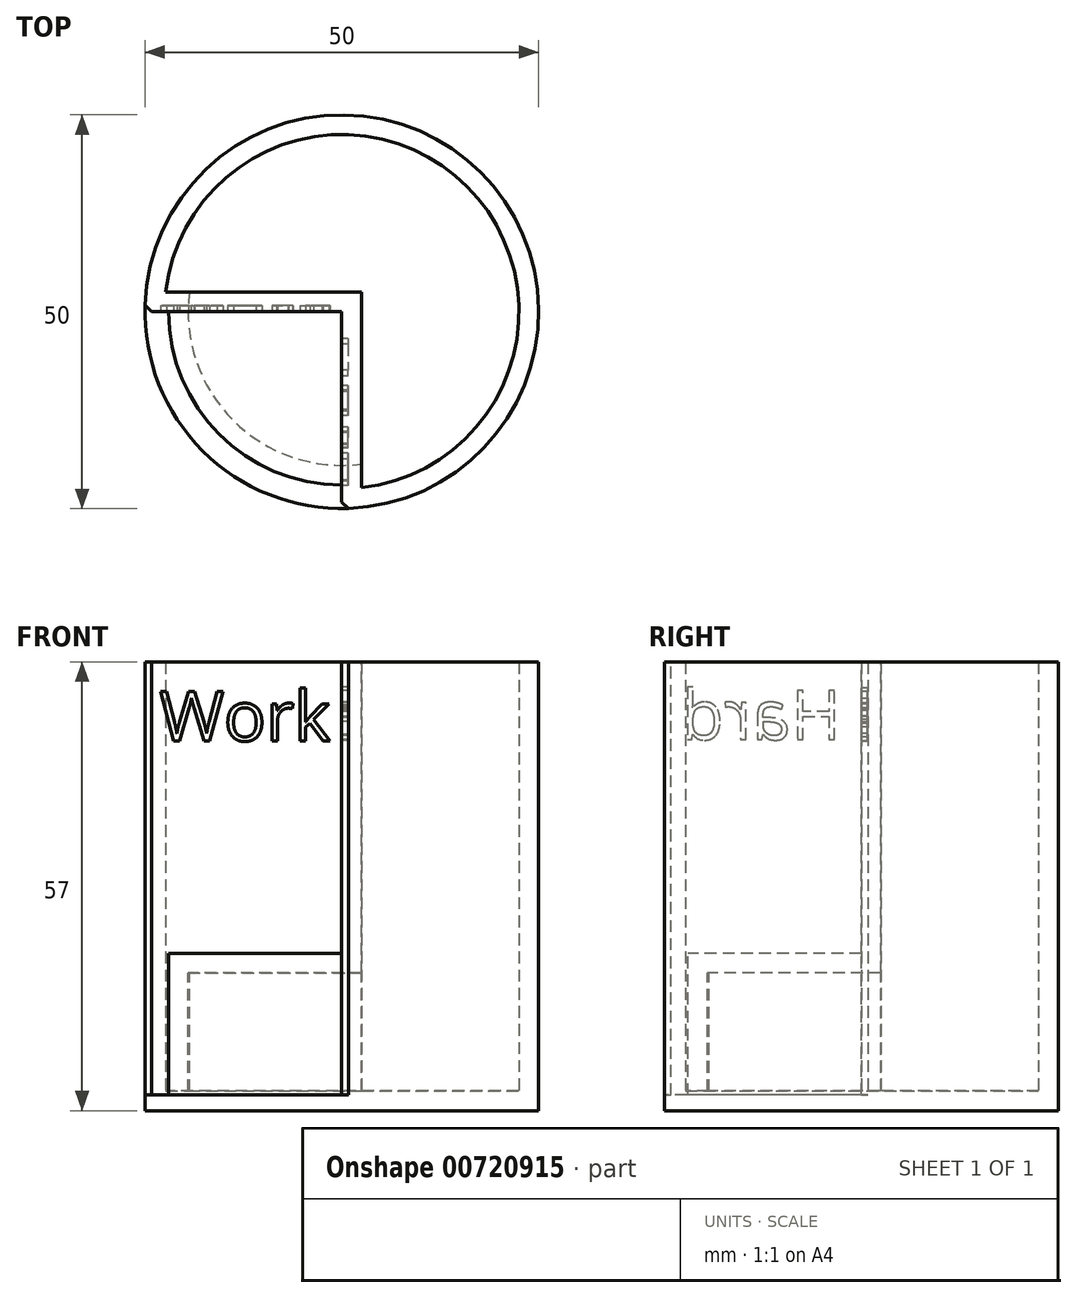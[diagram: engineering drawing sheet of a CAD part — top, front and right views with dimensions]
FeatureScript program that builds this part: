
annotation { "Feature Type Name" : "Feature", "Feature Type Description" : "" }
export const myFeature = defineFeature(function(context is Context, id is Id, definition is map)
    precondition{}
    {
        {
            var Q0;
            Q0=qCreatedBy(makeId("Top.planeOp"),FACE);
            var sketch = newSketch(context, id + "F0", { "sketchPlane" : qUnion([Q0])});
            skCircle(sketch, "E0", {"center": v(0, 0) * mm, "radius": 25 * mm});
            skSolve(sketch);
        }
        {
            var Q0;
            Q0=makeQuery(id+"F0.imprint","IMPRINT",FACE,{"disambiguationData":[TD([[makeQuery(id+"F0.imprint","IMPRINT",EDGE,{"derivedFrom":sQuery(id+"F0.wireOp",EDGE,"E0")}),1.0]])]});
            extrude(context, id + "F1", {"entities" : qUnion([Q0]), "depth" : 50 * mm, "offsetDistance" : 25 * mm});
        }
        {
            var Q0;
            Q0=makeQuery(id+"F1.opExtrude","CAP_FACE",FACE,{"disambiguationData":[OSD([sQuery(id+"F0.wireOp",EDGE,"E0")])],"isStart":false});
            var sketch = newSketch(context, id + "F2", { "sketchPlane" : qUnion([Q0])});
            skLineSegment(sketch, "E1.bottom", {"start": v(0, 0) * mm, "end": v(-35.4, 0) * mm});
            skLineSegment(sketch, "E1.top", {"start": v(0, -37.42) * mm, "end": v(-35.4, -37.42) * mm});
            skLineSegment(sketch, "E1.left", {"start": v(0, 0) * mm, "end": v(0, -37.42) * mm});
            skLineSegment(sketch, "E1.right", {"start": v(-35.4, 0) * mm, "end": v(-35.4, -37.42) * mm});
            skSolve(sketch);
        }
        {
            var Q0;
            {var subQ0=sQuery(id+"F2.wireOp",EDGE,"E1.left");var subQ1=sQuery(id+"F2.wireOp",EDGE,"E1.bottom");var subQ2=makeQuery(id+"F2.imprint","INTERSECT",VERTEX,{"derivedFrom":[subQ1,subQ0]});Q0=makeQuery(id+"F2.imprint","IMPRINT",FACE,{"disambiguationData":[TD([[makeQuery(id+"F2.imprint","IMPRINT",EDGE,{"disambiguationData":[TD([[subQ2,-1.0]])],"derivedFrom":subQ1}),1.0]])]});}
            extrude(context, id + "F3", {"entities" : qUnion([Q0]), "operationType" : NewBodyOperationType.REMOVE, "oppositeDirection" : true, "depth" : 30 * mm, "offsetDistance" : 25 * mm});
        }
        {
            var Q0;
            Q0=makeQuery(id+"F3.boolean.opBoolean","COPY",FACE,{"derivedFrom":makeQuery(id+"F3.opExtrude","CAP_FACE",FACE,{"disambiguationData":[OSD([sQuery(id+"F0.wireOp",EDGE,"E0"),sQuery(id+"F2.wireOp",EDGE,"E1.bottom"),sQuery(id+"F2.wireOp",EDGE,"E1.left")])],"isStart":false})});
            var sketch = newSketch(context, id + "F4", { "sketchPlane" : qUnion([Q0])});
            skArc(sketch, "E2", {"start": v(0, -22.02) * mm, "mid": v(-15.57, -15.57) * mm, "end": v(-22.02, 0) * mm});
            skSolve(sketch);
        }
        {
            var Q0;
            {var subQ0=sQuery(id+"F4.wireOp",EDGE,"E2");Q0=makeQuery(id+"F4.imprint","IMPRINT",FACE,{"disambiguationData":[TD([[makeQuery(id+"F4.imprint","IMPRINT",EDGE,{"derivedFrom":subQ0}),-1.0]])]});}
            var Q1;
            Q1=makeQuery(id+"F1.opExtrude","CAP_FACE",FACE,{"disambiguationData":[OSD([sQuery(id+"F0.wireOp",EDGE,"E0")])],"isStart":false});
            extrude(context, id + "F5", {"entities" : qUnion([Q0, Q1]), "operationType" : NewBodyOperationType.REMOVE, "oppositeDirection" : true, "depth" : 18 * mm, "offsetDistance" : 25 * mm});
        }
        {
            var Q0;
            Q0=makeQuery(id+"F5.boolean.opBoolean","COPY",FACE,{"derivedFrom":makeQuery(id+"F5.opExtrude","CAP_FACE",FACE,{"disambiguationData":[OSD([sQuery(id+"F0.wireOp",EDGE,"E0")])],"isStart":false})});
            shell(context, id + "F6", {"entities" : qUnion([Q0]), "thickness" : 2.5 * mm});
        }
        {
            var Q0;
            Q0=makeQuery(id+"F5.boolean.opBoolean","COPY",FACE,{"derivedFrom":makeQuery(id+"F5.opExtrude","CAP_FACE",FACE,{"disambiguationData":[OSD([sQuery(id+"F0.wireOp",EDGE,"E0")])],"isStart":false})});
            extrude(context, id + "F7", {"entities" : qUnion([Q0]), "operationType" : NewBodyOperationType.ADD, "depth" : 25 * mm, "offsetDistance" : 25 * mm});
        }
        {
            var Q0;
            Q0=makeQuery(id+"F3.boolean.opBoolean","COPY",EDGE,{"derivedFrom":makeQuery(id+"F3.opExtrude","CAP_EDGE",EDGE,{"disambiguationData":[OSD([sQuery(id+"F0.wireOp",EDGE,"E0")])],"isStart":false})});
            var Q1;
            Q1=makeQuery(id+"F5.boolean.opBoolean","COPY",EDGE,{"derivedFrom":makeQuery(id+"F5.opExtrude","CAP_EDGE",EDGE,{"disambiguationData":[OSD([sQuery(id+"F4.wireOp",EDGE,"E2")])],"isStart":true})});
            var Q2;
            {var subQ0=sQuery(id+"F2.wireOp",EDGE,"E1.left");var subQ1=sQuery(id+"F0.wireOp",EDGE,"E0");Q2=makeQuery(id+"F7.boolean.opBoolean","MERGE",EDGE,{"derivedFrom":[makeQuery(id+"F3.boolean.opBoolean","COPY",EDGE,{"derivedFrom":makeQuery(id+"F3.opExtrude","SWEPT_EDGE",EDGE,{"disambiguationData":[OSD([subQ1,subQ0])]})}),makeQuery(id+"F7.opExtrude","SWEPT_EDGE",EDGE,{"disambiguationData":[OSD([subQ1,subQ0]),TDD([makeQuery(id+"F5.boolean.opBoolean","COPY",VERTEX,{"derivedFrom":makeQuery(id+"F5.opExtrude","CAP_VERTEX",VERTEX,{"disambiguationData":[OSD([subQ1,subQ0])],"isStart":false})})])]})]});}
            var Q3;
            {var subQ0=sQuery(id+"F2.wireOp",EDGE,"E1.bottom");var subQ1=sQuery(id+"F0.wireOp",EDGE,"E0");Q3=makeQuery(id+"F7.boolean.opBoolean","MERGE",EDGE,{"derivedFrom":[makeQuery(id+"F3.boolean.opBoolean","COPY",EDGE,{"derivedFrom":makeQuery(id+"F3.opExtrude","SWEPT_EDGE",EDGE,{"disambiguationData":[OSD([subQ1,subQ0])]})}),makeQuery(id+"F7.opExtrude","SWEPT_EDGE",EDGE,{"disambiguationData":[OSD([subQ1,subQ0]),TDD([makeQuery(id+"F5.boolean.opBoolean","COPY",VERTEX,{"derivedFrom":makeQuery(id+"F5.opExtrude","CAP_VERTEX",VERTEX,{"disambiguationData":[OSD([subQ1,subQ0])],"isStart":false})})])]})]});}
            var Q4;
            {var subQ0=sQuery(id+"F2.wireOp",EDGE,"E1.bottom");Q4=makeQuery(id+"F7.opExtrude","CAP_EDGE",EDGE,{"disambiguationData":[OSD([subQ0]),TDD([makeQuery(id+"F5.boolean.opBoolean","COPY",EDGE,{"derivedFrom":makeQuery(id+"F5.opExtrude","CAP_EDGE",EDGE,{"disambiguationData":[OSD([subQ0]),TDD([makeQuery(id+"F3.boolean.opBoolean","COPY",EDGE,{"derivedFrom":makeQuery(id+"F3.opExtrude","CAP_EDGE",EDGE,{"disambiguationData":[OSD([subQ0])],"isStart":true})})])],"isStart":false})})])],"isStart":false});}
            var Q5;
            {var subQ0=sQuery(id+"F2.wireOp",EDGE,"E1.left");Q5=makeQuery(id+"F7.opExtrude","CAP_EDGE",EDGE,{"disambiguationData":[OSD([subQ0]),TDD([makeQuery(id+"F5.boolean.opBoolean","COPY",EDGE,{"derivedFrom":makeQuery(id+"F5.opExtrude","CAP_EDGE",EDGE,{"disambiguationData":[OSD([subQ0]),TDD([makeQuery(id+"F3.boolean.opBoolean","COPY",EDGE,{"derivedFrom":makeQuery(id+"F3.opExtrude","CAP_EDGE",EDGE,{"disambiguationData":[OSD([subQ0])],"isStart":true})})])],"isStart":false})})])],"isStart":false});}
            var Q6;
            {var subQ0=sQuery(id+"F2.wireOp",EDGE,"E1.left");Q6=makeQuery(id+"F7.opExtrude","CAP_EDGE",EDGE,{"disambiguationData":[OSD([subQ0]),TDD([makeQuery(id+"F6.opShell","OFFSET_EDGE",EDGE,{"disambiguationData":[OSD([subQ0])]})])],"isStart":false});}
            var Q7;
            {var subQ0=sQuery(id+"F0.wireOp",EDGE,"E0");Q7=makeQuery(id+"F7.opExtrude","CAP_EDGE",EDGE,{"disambiguationData":[OSD([subQ0]),TDD([makeQuery(id+"F6.opShell","OFFSET_EDGE",EDGE,{"disambiguationData":[OSD([subQ0]),TDD([makeQuery(id+"F5.boolean.opBoolean","COPY",EDGE,{"derivedFrom":makeQuery(id+"F5.opExtrude","CAP_EDGE",EDGE,{"disambiguationData":[OSD([subQ0])],"isStart":false})})])]})])],"isStart":false});}
            var Q8;
            {var subQ0=sQuery(id+"F0.wireOp",EDGE,"E0");Q8=makeQuery(id+"F7.opExtrude","CAP_EDGE",EDGE,{"disambiguationData":[OSD([subQ0]),TDD([makeQuery(id+"F5.boolean.opBoolean","COPY",EDGE,{"derivedFrom":makeQuery(id+"F5.opExtrude","CAP_EDGE",EDGE,{"disambiguationData":[OSD([subQ0])],"isStart":false})})])],"isStart":false});}
            var Q9;
            {var subQ0=sQuery(id+"F2.wireOp",EDGE,"E1.bottom");Q9=makeQuery(id+"F7.opExtrude","CAP_EDGE",EDGE,{"disambiguationData":[OSD([subQ0]),TDD([makeQuery(id+"F6.opShell","OFFSET_EDGE",EDGE,{"disambiguationData":[OSD([subQ0])]})])],"isStart":false});}
            chamfer(context, id + "F8", {"entities" : qUnion([Q0, Q1, Q2, Q3, Q4, Q5, Q6, Q7, Q8, Q9]), "width" : 0.8 * mm, "tangentPropagation" : true});
        }
        {
            var Q0;
            {var subQ0=sQuery(id+"F2.wireOp",EDGE,"E1.left");var subQ1=makeQuery(id+"F3.boolean.opBoolean","COPY",EDGE,{"derivedFrom":makeQuery(id+"F3.opExtrude","CAP_EDGE",EDGE,{"disambiguationData":[OSD([subQ0])],"isStart":false})});Q0=makeQuery(id+"F7.boolean.opBoolean","MERGE",FACE,{"derivedFrom":[makeQuery(id+"F5.boolean.opBoolean","MERGE",FACE,{"derivedFrom":[makeQuery(id+"F3.boolean.opBoolean","COPY",FACE,{"derivedFrom":makeQuery(id+"F3.opExtrude","SWEPT_FACE",FACE,{"disambiguationData":[OSD([subQ0])]})}),makeQuery(id+"F5.opExtrude","SWEPT_FACE",FACE,{"disambiguationData":[OSD([subQ0]),TDD([makeQuery(id+"F4.imprint","IMPRINT",EDGE,{"disambiguationData":[TD([[makeQuery(id+"F4.imprint","INTERSECT",VERTEX,{"derivedFrom":[makeQuery(id+"F3.boolean.opBoolean","COPY",EDGE,{"derivedFrom":makeQuery(id+"F3.opExtrude","CAP_EDGE",EDGE,{"disambiguationData":[OSD([sQuery(id+"F2.wireOp",EDGE,"E1.bottom")])],"isStart":false})}),subQ1]}),-1.0]])],"derivedFrom":subQ1})])]})]}),makeQuery(id+"F7.opExtrude","SWEPT_FACE",FACE,{"disambiguationData":[OSD([subQ0]),TDD([makeQuery(id+"F5.boolean.opBoolean","COPY",EDGE,{"derivedFrom":makeQuery(id+"F5.opExtrude","CAP_EDGE",EDGE,{"disambiguationData":[OSD([subQ0]),TDD([makeQuery(id+"F3.boolean.opBoolean","COPY",EDGE,{"derivedFrom":makeQuery(id+"F3.opExtrude","CAP_EDGE",EDGE,{"disambiguationData":[OSD([subQ0])],"isStart":true})})])],"isStart":false})})])]})]});}
            var sketch = newSketch(context, id + "F9", { "sketchPlane" : qUnion([Q0])});
            skText(sketch, "E3", { "text": "Hard", "fontName": "OpenSans-Regular.ttf"});
            const initialGuessF9  = {"E3": [0.00253, 0.04714, 1, 0, 0.00632]};
            skSetInitialGuess(sketch, initialGuessF9);
            skSolve(sketch);
        }
        {
            var Q0;
            {var subQ0=sQuery(id+"F2.wireOp",EDGE,"E1.bottom");var subQ1=makeQuery(id+"F3.boolean.opBoolean","COPY",EDGE,{"derivedFrom":makeQuery(id+"F3.opExtrude","CAP_EDGE",EDGE,{"disambiguationData":[OSD([subQ0])],"isStart":false})});Q0=makeQuery(id+"F7.boolean.opBoolean","MERGE",FACE,{"derivedFrom":[makeQuery(id+"F5.boolean.opBoolean","MERGE",FACE,{"derivedFrom":[makeQuery(id+"F3.boolean.opBoolean","COPY",FACE,{"derivedFrom":makeQuery(id+"F3.opExtrude","SWEPT_FACE",FACE,{"disambiguationData":[OSD([subQ0])]})}),makeQuery(id+"F5.opExtrude","SWEPT_FACE",FACE,{"disambiguationData":[OSD([subQ0]),TDD([makeQuery(id+"F4.imprint","IMPRINT",EDGE,{"disambiguationData":[TD([[makeQuery(id+"F4.imprint","INTERSECT",VERTEX,{"derivedFrom":[subQ1,makeQuery(id+"F3.boolean.opBoolean","COPY",EDGE,{"derivedFrom":makeQuery(id+"F3.opExtrude","CAP_EDGE",EDGE,{"disambiguationData":[OSD([sQuery(id+"F2.wireOp",EDGE,"E1.left")])],"isStart":false})})]}),-1.0]])],"derivedFrom":subQ1})])]})]}),makeQuery(id+"F7.opExtrude","SWEPT_FACE",FACE,{"disambiguationData":[OSD([subQ0]),TDD([makeQuery(id+"F5.boolean.opBoolean","COPY",EDGE,{"derivedFrom":makeQuery(id+"F5.opExtrude","CAP_EDGE",EDGE,{"disambiguationData":[OSD([subQ0]),TDD([makeQuery(id+"F3.boolean.opBoolean","COPY",EDGE,{"derivedFrom":makeQuery(id+"F3.opExtrude","CAP_EDGE",EDGE,{"disambiguationData":[OSD([subQ0])],"isStart":true})})])],"isStart":false})})])]})]});}
            var sketch = newSketch(context, id + "F10", { "sketchPlane" : qUnion([Q0])});
            skText(sketch, "E4", { "text": "Work", "fontName": "OpenSans-Regular.ttf"});
            const initialGuessF10  = {"E4": [-0.02314, 0.04697, 1, 0, 0.00635]};
            skSetInitialGuess(sketch, initialGuessF10);
            skSolve(sketch);
        }
        {
            var Q0;
            Q0=makeQuery(id+"F10.imprint","IMPRINT",FACE,{"disambiguationData":[TD([[makeQuery(id+"F10.imprint","IMPRINT",EDGE,{"derivedFrom":sQuery(id+"F10.wireOp",EDGE,"E4.sketch_text.stroke-0")}),-1.0]])]});
            var Q1;
            Q1=makeQuery(id+"F10.imprint","IMPRINT",FACE,{"disambiguationData":[TD([[makeQuery(id+"F10.imprint","IMPRINT",EDGE,{"derivedFrom":sQuery(id+"F10.wireOp",EDGE,"E4.sketch_text.stroke-20")}),-1.0]])]});
            var Q2;
            Q2=makeQuery(id+"F10.imprint","IMPRINT",FACE,{"disambiguationData":[TD([[makeQuery(id+"F10.imprint","IMPRINT",EDGE,{"derivedFrom":sQuery(id+"F10.wireOp",EDGE,"E4.sketch_text.stroke-37")}),-1.0]])]});
            var Q3;
            Q3=makeQuery(id+"F10.imprint","IMPRINT",FACE,{"disambiguationData":[TD([[makeQuery(id+"F10.imprint","IMPRINT",EDGE,{"derivedFrom":sQuery(id+"F10.wireOp",EDGE,"E4.sketch_text.stroke-50")}),-1.0]])]});
            extrude(context, id + "F11", {"entities" : qUnion([Q0, Q1, Q2, Q3]), "operationType" : NewBodyOperationType.REMOVE, "oppositeDirection" : true, "depth" : 0.8 * mm, "offsetDistance" : 25 * mm});
        }
        {
            var Q0;
            Q0=makeQuery(id+"F9.imprint","IMPRINT",FACE,{"disambiguationData":[TD([[makeQuery(id+"F9.imprint","IMPRINT",EDGE,{"derivedFrom":sQuery(id+"F9.wireOp",EDGE,"E3.sketch_text.stroke-0")}),-1.0]])]});
            var Q1;
            Q1=makeQuery(id+"F9.imprint","IMPRINT",FACE,{"disambiguationData":[TD([[makeQuery(id+"F9.imprint","IMPRINT",EDGE,{"derivedFrom":sQuery(id+"F9.wireOp",EDGE,"E3.sketch_text.stroke-12")}),-1.0]])]});
            var Q2;
            Q2=makeQuery(id+"F9.imprint","IMPRINT",FACE,{"disambiguationData":[TD([[makeQuery(id+"F9.imprint","IMPRINT",EDGE,{"derivedFrom":sQuery(id+"F9.wireOp",EDGE,"E3.sketch_text.stroke-39")}),-1.0]])]});
            var Q3;
            Q3=makeQuery(id+"F9.imprint","IMPRINT",FACE,{"disambiguationData":[TD([[makeQuery(id+"F9.imprint","IMPRINT",EDGE,{"derivedFrom":sQuery(id+"F9.wireOp",EDGE,"E3.sketch_text.stroke-52")}),-1.0]])]});
            extrude(context, id + "F12", {"entities" : qUnion([Q0, Q1, Q2, Q3]), "operationType" : NewBodyOperationType.REMOVE, "oppositeDirection" : true, "depth" : 0.8 * mm, "offsetDistance" : 25 * mm});
        }
    });
